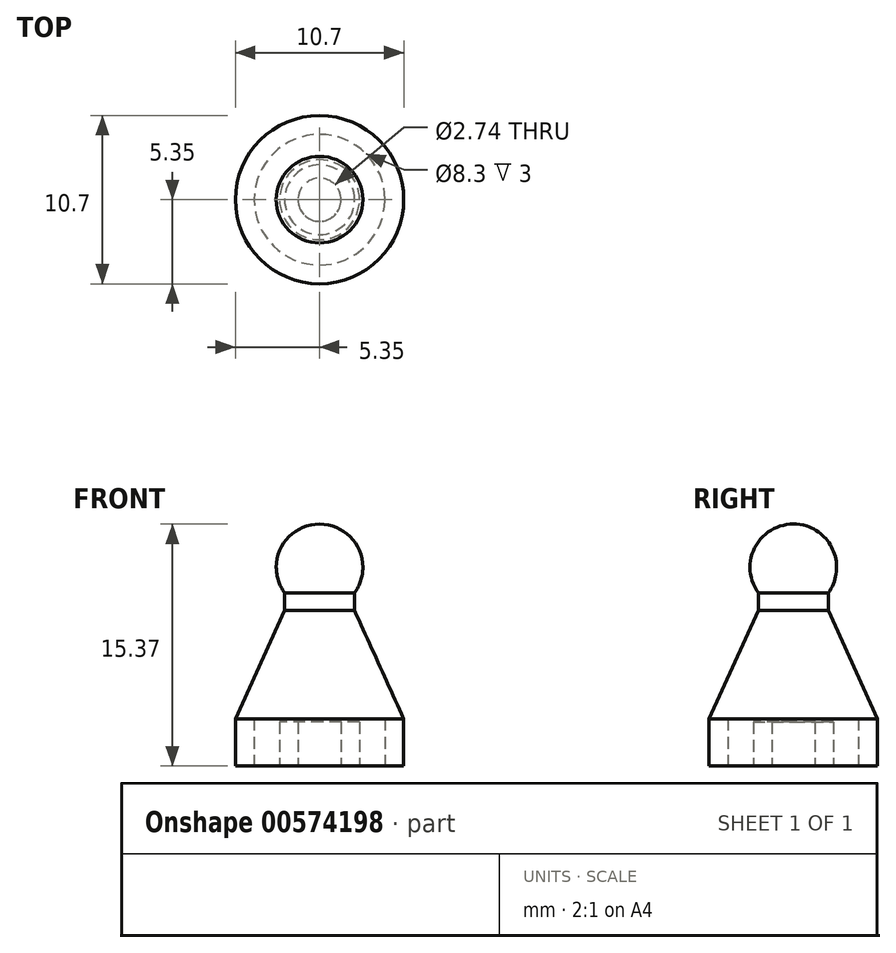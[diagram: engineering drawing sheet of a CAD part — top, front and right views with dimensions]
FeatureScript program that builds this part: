
annotation { "Feature Type Name" : "Feature", "Feature Type Description" : "" }
export const myFeature = defineFeature(function(context is Context, id is Id, definition is map)
    precondition{}
    {
        {
            var Q0;
            Q0=qCreatedBy(makeId("Top.planeOp"),FACE);
            var sketch = newSketch(context, id + "F0", { "sketchPlane" : qUnion([Q0])});
            skCircle(sketch, "E0", {"center": v(0, 0) * mm, "radius": 5.34 * mm});
            skSolve(sketch);
        }
        {
            var Q0;
            Q0=qCreatedBy(makeId("Top.planeOp"),FACE);
            cPlane(context, id + "F1", {"entities" : qUnion([Q0]), "cplaneType" : CPlaneType.OFFSET, "offset" : 9.87 * mm, "width" : 150 * mm, "height" : 150 * mm});
        }
        {
            var Q0;
            Q0=qCreatedBy(id+"F1.planeOp",FACE);
            var sketch = newSketch(context, id + "F2", { "sketchPlane" : qUnion([Q0])});
            skPoint(sketch, "E1", {"position": v(0, 0) * mm});
            skCircle(sketch, "E2", {"center": v(0, 0) * mm, "radius": 2.22 * mm});
            skSolve(sketch);
        }
        {
            var Q0;
            Q0=makeQuery(id+"F0.imprint","IMPRINT",FACE,{"disambiguationData":[TD([[makeQuery(id+"F0.imprint","IMPRINT",EDGE,{"derivedFrom":sQuery(id+"F0.wireOp",EDGE,"E0")}),1.0]])]});
            extrude(context, id + "F3", {"entities" : qUnion([Q0]), "depth" : 3 * mm, "offsetDistance" : 25 * mm});
        }
        {
            var Q1;
            Q1=makeQuery(id+"F3.opExtrude","CAP_FACE",FACE,{"disambiguationData":[OSD([sQuery(id+"F0.wireOp",EDGE,"E0")])],"isStart":false});
            var Q2;
            Q2=makeQuery(id+"F2.imprint","IMPRINT",FACE,{"disambiguationData":[TD([[makeQuery(id+"F2.imprint","IMPRINT",EDGE,{"derivedFrom":sQuery(id+"F2.wireOp",EDGE,"E2")}),1.0]])]});
            loft(context, id + "F4", {"operationType" : NewBodyOperationType.ADD, "sheetProfilesArray" : [{ "sheetProfileEntities" : qUnion([Q1]) }, { "sheetProfileEntities" : qUnion([Q2]) }]});
        }
        {
            var Q0;
            Q0=qCreatedBy(id+"F1.planeOp",FACE);
            cPlane(context, id + "F5", {"entities" : qUnion([Q0]), "cplaneType" : CPlaneType.OFFSET, "offset" : (5.5 / 2) * mm, "width" : 150 * mm, "height" : 150 * mm});
        }
        {
            var Q0;
            Q0=qCreatedBy(id+"F5.planeOp",FACE);
            var sketch = newSketch(context, id + "F6", { "sketchPlane" : qUnion([Q0])});
            skPoint(sketch, "E3", {"position": v(0, 0) * mm});
            skArc(sketch, "E4", {"start": v(2.75, 0) * mm, "mid": v(0, 2.75) * mm, "end": v(-2.75, 0) * mm});
            skLineSegment(sketch, "E5", {"start": v(7.18, 0) * mm, "end": v(-9.15, 0) * mm, "construction": true});
            skLineSegment(sketch, "E6", {"start": v(-2.75, 0) * mm, "end": v(2.75, 0) * mm});
            skSolve(sketch);
        }
        {
            var Q0;
            Q0=makeQuery(id+"F6.imprint","IMPRINT",FACE,{"disambiguationData":[TD([[makeQuery(id+"F6.imprint","IMPRINT",EDGE,{"derivedFrom":sQuery(id+"F6.wireOp",EDGE,"E4")}),1.0]])]});
            var Q1;
            Q1=sQuery(id+"F6.wireOp",EDGE,"E5");
            revolve(context, id + "F7", {"entities" : qUnion([Q0]), "axis" : qUnion([Q1]), "revolveType" : RevolveType.FULL});
        }
        {
            var Q0;
            Q0=makeQuery(id+"F2.imprint","IMPRINT",FACE,{"disambiguationData":[TD([[makeQuery(id+"F2.imprint","IMPRINT",EDGE,{"derivedFrom":sQuery(id+"F2.wireOp",EDGE,"E2")}),1.0]])]});
            extrude(context, id + "F8", {"entities" : qUnion([Q0]), "operationType" : NewBodyOperationType.ADD, "endBound" : BoundingType.UP_TO_NEXT, "depth" : 25 * mm, "offsetDistance" : 25 * mm});
        }
        {
            var Q0;
            Q0=qCreatedBy(makeId("Top.planeOp"),FACE);
            var sketch = newSketch(context, id + "F9", { "sketchPlane" : qUnion([Q0])});
            skCircle(sketch, "E7", {"center": v(0, 0) * mm, "radius": 4.15 * mm});
            skSolve(sketch);
        }
        {
            var Q0;
            Q0 = qSketchRegion(id + "F9", true);
            extrude(context, id + "F10", {"entities" : qUnion([Q0]), "operationType" : NewBodyOperationType.REMOVE, "depth" : 3 * mm, "offsetDistance" : 25 * mm});
        }
        {
            var Q0;
            Q0=qCreatedBy(makeId("Top.planeOp"),FACE);
            var sketch = newSketch(context, id + "F11", { "sketchPlane" : qUnion([Q0])});
            skCircle(sketch, "E8", {"center": v(0, 0) * mm, "radius": 2.54 * mm});
            skSolve(sketch);
        }
        {
            var Q0;
            Q0 = qSketchRegion(id + "F11", true);
            extrude(context, id + "F12", {"entities" : qUnion([Q0]), "depth" : 2.8 * mm, "offsetDistance" : 25 * mm});
        }
        {
            var Q0;
            Q0=makeQuery(id+"F12.opExtrude","CAP_FACE",FACE,{"disambiguationData":[OSD([sQuery(id+"F11.wireOp",EDGE,"E8")])],"isStart":true});
            var sketch = newSketch(context, id + "F13", { "sketchPlane" : qUnion([Q0])});
            skCircle(sketch, "E9", {"center": v(0, 0) * mm, "radius": 1.37 * mm});
            skSolve(sketch);
        }
        {
            var Q0;
            Q0 = qSketchRegion(id + "F13", true);
            extrude(context, id + "F14", {"entities" : qUnion([Q0]), "operationType" : NewBodyOperationType.REMOVE, "oppositeDirection" : true, "depth" : 2.9 * mm, "offsetDistance" : 25 * mm});
        }
    });
